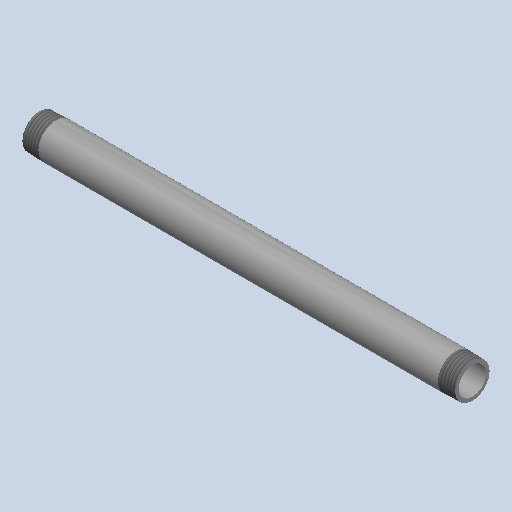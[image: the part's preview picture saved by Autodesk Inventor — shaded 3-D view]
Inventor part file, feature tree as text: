
AUTODESK INVENTOR PART (.ipt)
format: ipt  version: 2025 (Build 290162000, 162)  size: 177,152 bytes
history: native  units: mm (DEFAULTED — no unit token found)
features: other x8, revolve x1
ambient origin geometry x8: Origin, YZ Plane, XZ Plane, XY Plane, X Axis, Y Axis, Z Axis, Center Point
bodies: Solid1 (feature_tree)
feature tree (9):
  revolve  "Revolution1"  [1 undecoded]
  other  "Work Axis1"
  other  "Work Point5"
  other  "Work Axis2"
  other  "Work Point6"
  other  "Work Axis3"
  other  "Work Axis4"
  other  "Work Point7"
  other  "Work Point8"
note: 1 required parameter value undecoded (feature->parameter linkage not recoverable at this tier; creation-order binding heuristic only, values carry confidence <= 0.55)
